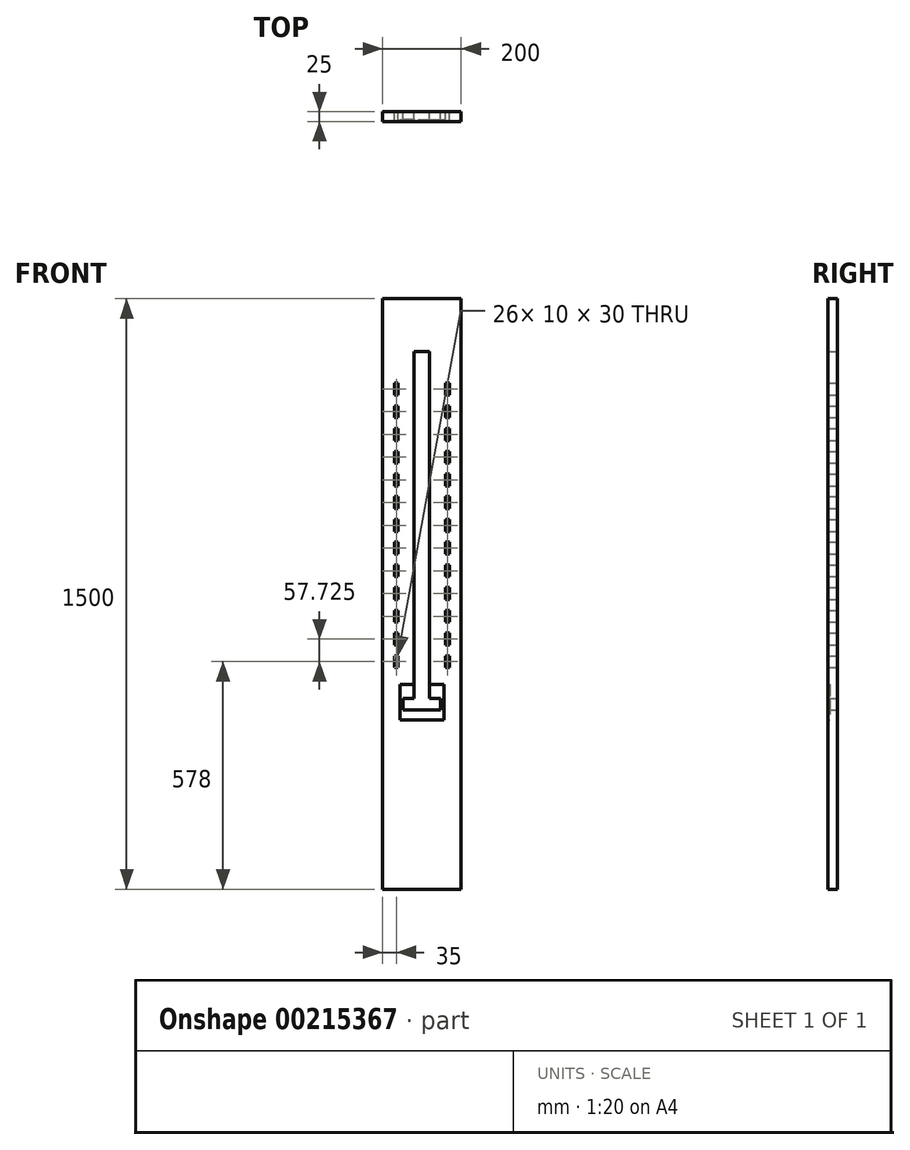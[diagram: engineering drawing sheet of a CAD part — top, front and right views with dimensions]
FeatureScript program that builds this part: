
annotation { "Feature Type Name" : "Feature", "Feature Type Description" : "" }
export const myFeature = defineFeature(function(context is Context, id is Id, definition is map)
    precondition{}
    {
        {
            var Q0;
            Q0=qCreatedBy(makeId("Front.planeOp"),FACE);
            var sketch = newSketch(context, id + "F0", { "sketchPlane" : qUnion([Q0])});
            skLineSegment(sketch, "E0.bottom", {"start": v(-100, 750) * mm, "end": v(100, 750) * mm});
            skLineSegment(sketch, "E0.top", {"start": v(-100, -750) * mm, "end": v(100, -750) * mm});
            skLineSegment(sketch, "E0.left", {"start": v(-100, 750) * mm, "end": v(-100, -750) * mm});
            skLineSegment(sketch, "E0.right", {"start": v(100, 750) * mm, "end": v(100, -750) * mm});
            skPoint(sketch, "E0.middle", {"position": v(0, 0) * mm});
            skPoint(sketch, "E1.endSnap0", {"position": v(0, -750) * mm});
            skLineSegment(sketch, "E2.bottom", {"start": v(-60, -187) * mm, "end": v(-70, -187) * mm});
            skLineSegment(sketch, "E2.top", {"start": v(-60, -157) * mm, "end": v(-70, -157) * mm});
            skLineSegment(sketch, "E2.left", {"start": v(-60, -187) * mm, "end": v(-60, -157) * mm});
            skLineSegment(sketch, "E2.right", {"start": v(-70, -187) * mm, "end": v(-70, -157) * mm});
            skLineSegment(sketch, "E3.bottom", {"start": v(-60, -129.27) * mm, "end": v(-70, -129.27) * mm});
            skLineSegment(sketch, "E3.top", {"start": v(-60, -99.27) * mm, "end": v(-70, -99.27) * mm});
            skLineSegment(sketch, "E3.left", {"start": v(-60, -129.27) * mm, "end": v(-60, -99.27) * mm});
            skLineSegment(sketch, "E3.right", {"start": v(-70, -129.27) * mm, "end": v(-70, -99.27) * mm});
            skLineSegment(sketch, "E4.bottom", {"start": v(-60, -71.55) * mm, "end": v(-70, -71.55) * mm});
            skLineSegment(sketch, "E4.top", {"start": v(-60, -41.55) * mm, "end": v(-70, -41.55) * mm});
            skLineSegment(sketch, "E4.left", {"start": v(-60, -71.55) * mm, "end": v(-60, -41.55) * mm});
            skLineSegment(sketch, "E4.right", {"start": v(-70, -71.55) * mm, "end": v(-70, -41.55) * mm});
            skLineSegment(sketch, "E5.bottom", {"start": v(-60, -13.82) * mm, "end": v(-70, -13.82) * mm});
            skLineSegment(sketch, "E5.top", {"start": v(-60, 16.18) * mm, "end": v(-70, 16.18) * mm});
            skLineSegment(sketch, "E5.left", {"start": v(-60, -13.82) * mm, "end": v(-60, 16.18) * mm});
            skLineSegment(sketch, "E5.right", {"start": v(-70, -13.82) * mm, "end": v(-70, 16.18) * mm});
            skLineSegment(sketch, "E6.bottom", {"start": v(-60, 43.9) * mm, "end": v(-70, 43.9) * mm});
            skLineSegment(sketch, "E6.top", {"start": v(-60, 73.9) * mm, "end": v(-70, 73.9) * mm});
            skLineSegment(sketch, "E6.left", {"start": v(-60, 43.9) * mm, "end": v(-60, 73.9) * mm});
            skLineSegment(sketch, "E6.right", {"start": v(-70, 43.9) * mm, "end": v(-70, 73.9) * mm});
            skLineSegment(sketch, "E7.bottom", {"start": v(-60, 101.63) * mm, "end": v(-70, 101.63) * mm});
            skLineSegment(sketch, "E7.top", {"start": v(-60, 131.63) * mm, "end": v(-70, 131.63) * mm});
            skLineSegment(sketch, "E7.left", {"start": v(-60, 101.63) * mm, "end": v(-60, 131.63) * mm});
            skLineSegment(sketch, "E7.right", {"start": v(-70, 101.63) * mm, "end": v(-70, 131.63) * mm});
            skLineSegment(sketch, "E8.bottom", {"start": v(-60, 159.35) * mm, "end": v(-70, 159.35) * mm});
            skLineSegment(sketch, "E8.top", {"start": v(-60, 189.35) * mm, "end": v(-70, 189.35) * mm});
            skLineSegment(sketch, "E8.left", {"start": v(-60, 159.35) * mm, "end": v(-60, 189.35) * mm});
            skLineSegment(sketch, "E8.right", {"start": v(-70, 159.35) * mm, "end": v(-70, 189.35) * mm});
            skLineSegment(sketch, "E9.bottom", {"start": v(-60, 217.08) * mm, "end": v(-70, 217.08) * mm});
            skLineSegment(sketch, "E9.top", {"start": v(-60, 247.08) * mm, "end": v(-70, 247.08) * mm});
            skLineSegment(sketch, "E9.left", {"start": v(-60, 217.08) * mm, "end": v(-60, 247.08) * mm});
            skLineSegment(sketch, "E9.right", {"start": v(-70, 217.08) * mm, "end": v(-70, 247.08) * mm});
            skLineSegment(sketch, "E10.bottom", {"start": v(-60, 274.8) * mm, "end": v(-70, 274.8) * mm});
            skLineSegment(sketch, "E10.top", {"start": v(-60, 304.8) * mm, "end": v(-70, 304.8) * mm});
            skLineSegment(sketch, "E10.left", {"start": v(-60, 274.8) * mm, "end": v(-60, 304.8) * mm});
            skLineSegment(sketch, "E10.right", {"start": v(-70, 274.8) * mm, "end": v(-70, 304.8) * mm});
            skLineSegment(sketch, "E11.bottom", {"start": v(-60, 332.53) * mm, "end": v(-70, 332.53) * mm});
            skLineSegment(sketch, "E11.top", {"start": v(-60, 362.53) * mm, "end": v(-70, 362.53) * mm});
            skLineSegment(sketch, "E11.left", {"start": v(-60, 332.53) * mm, "end": v(-60, 362.53) * mm});
            skLineSegment(sketch, "E11.right", {"start": v(-70, 332.53) * mm, "end": v(-70, 362.53) * mm});
            skLineSegment(sketch, "E12.bottom", {"start": v(-60, 390.25) * mm, "end": v(-70, 390.25) * mm});
            skLineSegment(sketch, "E12.top", {"start": v(-60, 420.25) * mm, "end": v(-70, 420.25) * mm});
            skLineSegment(sketch, "E12.left", {"start": v(-60, 390.25) * mm, "end": v(-60, 420.25) * mm});
            skLineSegment(sketch, "E12.right", {"start": v(-70, 390.25) * mm, "end": v(-70, 420.25) * mm});
            skLineSegment(sketch, "E13.bottom", {"start": v(-60, 447.98) * mm, "end": v(-70, 447.98) * mm});
            skLineSegment(sketch, "E13.top", {"start": v(-60, 477.98) * mm, "end": v(-70, 477.98) * mm});
            skLineSegment(sketch, "E13.left", {"start": v(-60, 447.98) * mm, "end": v(-60, 477.98) * mm});
            skLineSegment(sketch, "E13.right", {"start": v(-70, 447.98) * mm, "end": v(-70, 477.98) * mm});
            skLineSegment(sketch, "E14.bottom", {"start": v(-60, 505.7) * mm, "end": v(-70, 505.7) * mm});
            skLineSegment(sketch, "E14.top", {"start": v(-60, 535.7) * mm, "end": v(-70, 535.7) * mm});
            skLineSegment(sketch, "E14.left", {"start": v(-60, 505.7) * mm, "end": v(-60, 535.7) * mm});
            skLineSegment(sketch, "E14.right", {"start": v(-70, 505.7) * mm, "end": v(-70, 535.7) * mm});
            skLineSegment(sketch, "E15", {"start": v(-20, -230) * mm, "end": v(-56, -230) * mm});
            skLineSegment(sketch, "E16", {"start": v(-56, -230) * mm, "end": v(-56, -320) * mm});
            skLineSegment(sketch, "E17.MirrorCS", {"start": v(20, -230) * mm, "end": v(56, -230) * mm});
            skLineSegment(sketch, "E18", {"start": v(-56, -320) * mm, "end": v(56, -320) * mm});
            skLineSegment(sketch, "E19", {"start": v(-20, -230) * mm, "end": v(-20, -265) * mm});
            skLineSegment(sketch, "E20", {"start": v(-20, -265) * mm, "end": v(-48, -265) * mm});
            skLineSegment(sketch, "E21", {"start": v(-48, -265) * mm, "end": v(-48, -295) * mm});
            skLineSegment(sketch, "E22.MirrorCS", {"start": v(20, -230) * mm, "end": v(20, -265) * mm});
            skLineSegment(sketch, "E23.MirrorCS", {"start": v(20, -265) * mm, "end": v(48, -265) * mm});
            skLineSegment(sketch, "E24.MirrorCS", {"start": v(48, -265) * mm, "end": v(48, -295) * mm});
            skLineSegment(sketch, "E25", {"start": v(-48, -295) * mm, "end": v(48, -295) * mm});
            skLineSegment(sketch, "E26", {"start": v(56, -230) * mm, "end": v(56, -320) * mm});
            skPoint(sketch, "E27", {"position": v(-20, 615.7) * mm});
            skLineSegment(sketch, "E28", {"start": v(-20, 615.7) * mm, "end": v(20, 615.7) * mm});
            skLineSegment(sketch, "E29", {"start": v(-20, 615.7) * mm, "end": v(-20, -230) * mm});
            skLineSegment(sketch, "E30", {"start": v(20, -230) * mm, "end": v(20, 615.7) * mm});
            skLineSegment(sketch, "E31.MirrorCS", {"start": v(60, -187) * mm, "end": v(70, -187) * mm});
            skLineSegment(sketch, "E32.MirrorCS", {"start": v(60, -41.55) * mm, "end": v(70, -41.55) * mm});
            skLineSegment(sketch, "E33.MirrorCS", {"start": v(60, 159.35) * mm, "end": v(70, 159.35) * mm});
            skLineSegment(sketch, "E34.MirrorCS", {"start": v(60, 390.25) * mm, "end": v(70, 390.25) * mm});
            skLineSegment(sketch, "E35.MirrorCS", {"start": v(60, 332.53) * mm, "end": v(70, 332.53) * mm});
            skLineSegment(sketch, "E36.MirrorCS", {"start": v(60, 101.63) * mm, "end": v(70, 101.63) * mm});
            skLineSegment(sketch, "E37.MirrorCS", {"start": v(60, -157) * mm, "end": v(70, -157) * mm});
            skLineSegment(sketch, "E38.MirrorCS", {"start": v(60, 362.53) * mm, "end": v(70, 362.53) * mm});
            skLineSegment(sketch, "E39.MirrorCS", {"start": v(60, 131.63) * mm, "end": v(70, 131.63) * mm});
            skLineSegment(sketch, "E40.MirrorCS", {"start": v(60, -129.27) * mm, "end": v(70, -129.27) * mm});
            skLineSegment(sketch, "E41.MirrorCS", {"start": v(60, -99.27) * mm, "end": v(70, -99.27) * mm});
            skLineSegment(sketch, "E42.MirrorCS", {"start": v(60, -71.55) * mm, "end": v(70, -71.55) * mm});
            skLineSegment(sketch, "E43.MirrorCS", {"start": v(60, 43.9) * mm, "end": v(70, 43.9) * mm});
            skLineSegment(sketch, "E44.MirrorCS", {"start": v(60, 505.7) * mm, "end": v(70, 505.7) * mm});
            skLineSegment(sketch, "E45.MirrorCS", {"start": v(60, 274.8) * mm, "end": v(70, 274.8) * mm});
            skLineSegment(sketch, "E46.MirrorCS", {"start": v(60, -13.82) * mm, "end": v(70, -13.82) * mm});
            skLineSegment(sketch, "E47.MirrorCS", {"start": v(60, 447.98) * mm, "end": v(70, 447.98) * mm});
            skLineSegment(sketch, "E48.MirrorCS", {"start": v(60, 217.08) * mm, "end": v(70, 217.08) * mm});
            skLineSegment(sketch, "E49.MirrorCS", {"start": v(60, 16.18) * mm, "end": v(70, 16.18) * mm});
            skLineSegment(sketch, "E50.MirrorCS", {"start": v(60, 247.08) * mm, "end": v(70, 247.08) * mm});
            skLineSegment(sketch, "E51.MirrorCS", {"start": v(60, 477.98) * mm, "end": v(70, 477.98) * mm});
            skLineSegment(sketch, "E52.MirrorCS", {"start": v(60, 73.9) * mm, "end": v(70, 73.9) * mm});
            skLineSegment(sketch, "E53.MirrorCS", {"start": v(60, 535.7) * mm, "end": v(70, 535.7) * mm});
            skLineSegment(sketch, "E54.MirrorCS", {"start": v(60, 304.8) * mm, "end": v(70, 304.8) * mm});
            skLineSegment(sketch, "E55.MirrorCS", {"start": v(60, 420.25) * mm, "end": v(70, 420.25) * mm});
            skLineSegment(sketch, "E56.MirrorCS", {"start": v(60, 189.35) * mm, "end": v(70, 189.35) * mm});
            skLineSegment(sketch, "E57.MirrorCS", {"start": v(70, -71.55) * mm, "end": v(70, -41.55) * mm});
            skLineSegment(sketch, "E58.MirrorCS", {"start": v(60, -71.55) * mm, "end": v(60, -41.55) * mm});
            skLineSegment(sketch, "E59.MirrorCS", {"start": v(70, 159.35) * mm, "end": v(70, 189.35) * mm});
            skLineSegment(sketch, "E60.MirrorCS", {"start": v(70, 390.25) * mm, "end": v(70, 420.25) * mm});
            skLineSegment(sketch, "E61.MirrorCS", {"start": v(60, 159.35) * mm, "end": v(60, 189.35) * mm});
            skLineSegment(sketch, "E62.MirrorCS", {"start": v(60, 390.25) * mm, "end": v(60, 420.25) * mm});
            skLineSegment(sketch, "E63.MirrorCS", {"start": v(60, 274.8) * mm, "end": v(60, 304.8) * mm});
            skLineSegment(sketch, "E64.MirrorCS", {"start": v(70, 505.7) * mm, "end": v(70, 535.7) * mm});
            skLineSegment(sketch, "E65.MirrorCS", {"start": v(70, 274.8) * mm, "end": v(70, 304.8) * mm});
            skLineSegment(sketch, "E66.MirrorCS", {"start": v(70, 43.9) * mm, "end": v(70, 73.9) * mm});
            skLineSegment(sketch, "E67.MirrorCS", {"start": v(70, -13.82) * mm, "end": v(70, 16.18) * mm});
            skLineSegment(sketch, "E68.MirrorCS", {"start": v(60, -187) * mm, "end": v(60, -157) * mm});
            skLineSegment(sketch, "E69.MirrorCS", {"start": v(70, -187) * mm, "end": v(70, -157) * mm});
            skLineSegment(sketch, "E70.MirrorCS", {"start": v(70, 447.98) * mm, "end": v(70, 477.98) * mm});
            skLineSegment(sketch, "E71.MirrorCS", {"start": v(70, 217.08) * mm, "end": v(70, 247.08) * mm});
            skLineSegment(sketch, "E72.MirrorCS", {"start": v(60, -129.27) * mm, "end": v(60, -99.27) * mm});
            skLineSegment(sketch, "E73.MirrorCS", {"start": v(70, -129.27) * mm, "end": v(70, -99.27) * mm});
            skLineSegment(sketch, "E74.MirrorCS", {"start": v(60, 332.53) * mm, "end": v(60, 362.53) * mm});
            skLineSegment(sketch, "E75.MirrorCS", {"start": v(60, 101.63) * mm, "end": v(60, 131.63) * mm});
            skLineSegment(sketch, "E76.MirrorCS", {"start": v(60, -13.82) * mm, "end": v(60, 16.18) * mm});
            skLineSegment(sketch, "E77.MirrorCS", {"start": v(60, 447.98) * mm, "end": v(60, 477.98) * mm});
            skLineSegment(sketch, "E78.MirrorCS", {"start": v(60, 217.08) * mm, "end": v(60, 247.08) * mm});
            skLineSegment(sketch, "E79.MirrorCS", {"start": v(70, 332.53) * mm, "end": v(70, 362.53) * mm});
            skLineSegment(sketch, "E80.MirrorCS", {"start": v(70, 101.63) * mm, "end": v(70, 131.63) * mm});
            skLineSegment(sketch, "E81.MirrorCS", {"start": v(60, 43.9) * mm, "end": v(60, 73.9) * mm});
            skLineSegment(sketch, "E82.MirrorCS", {"start": v(60, 505.7) * mm, "end": v(60, 535.7) * mm});
            skSolve(sketch);
        }
        {
            var Q0;
            Q0 = qSketchRegion(id + "F0", true);
            extrude(context, id + "F1", {"entities" : qUnion([Q0]), "depth" : 25 * mm});
        }
        {
            var Q0;
            Q0=makeQuery(id+"F0.imprint","IMPRINT",FACE,{"disambiguationData":[TD([[makeQuery(id+"F0.imprint","IMPRINT",EDGE,{"derivedFrom":sQuery(id+"F0.wireOp",EDGE,"E15")}),1.0]])]});
            extrude(context, id + "F2", {"entities" : qUnion([Q0]), "operationType" : NewBodyOperationType.ADD, "depth" : 20 * mm});
        }
    });
